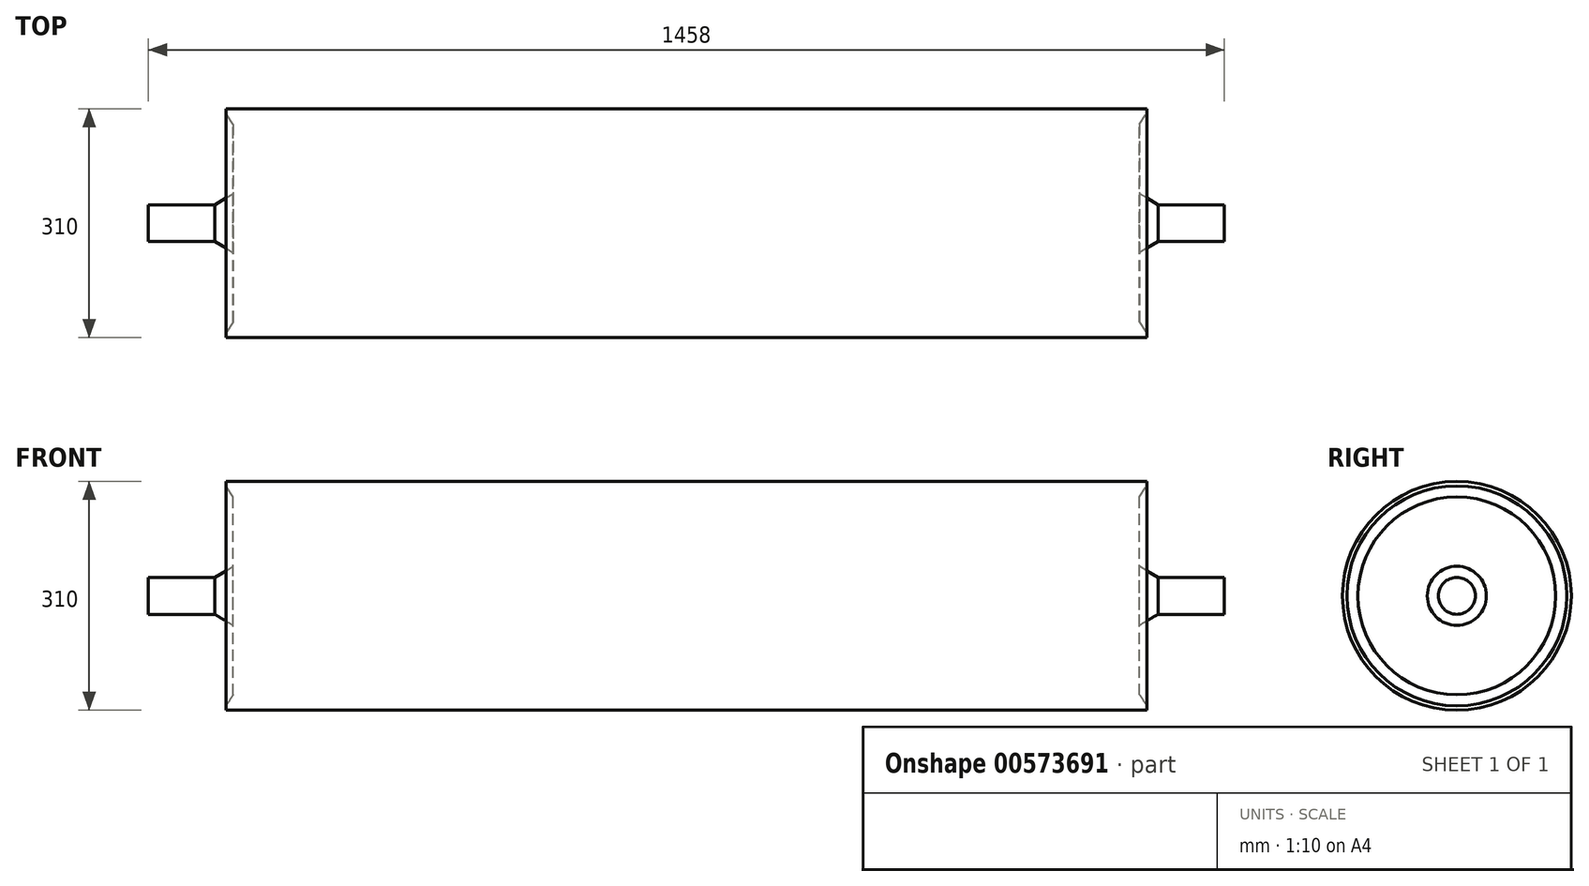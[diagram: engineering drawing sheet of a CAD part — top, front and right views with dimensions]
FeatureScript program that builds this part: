
annotation { "Feature Type Name" : "Feature", "Feature Type Description" : "" }
export const myFeature = defineFeature(function(context is Context, id is Id, definition is map)
    precondition{}
    {
        {
            var Q0;
            Q0=qCreatedBy(makeId("Front.planeOp"),FACE);
            var sketch = newSketch(context, id + "F0", { "sketchPlane" : qUnion([Q0])});
            skLineSegment(sketch, "E0.0", {"start": v(0, 155) * mm, "end": v(-614, 155) * mm});
            skLineSegment(sketch, "E1.0", {"start": v(0, 155) * mm, "end": v(624, 155) * mm});
            skLineSegment(sketch, "E2.0", {"start": v(614, 155) * mm, "end": v(614, 0) * mm});
            skLineSegment(sketch, "E3.0", {"start": v(-614, 155) * mm, "end": v(-614, 0) * mm});
            skLineSegment(sketch, "E4.0", {"start": v(614, 25) * mm, "end": v(729, 25) * mm});
            skLineSegment(sketch, "E5", {"start": v(729, 25) * mm, "end": v(729, 0) * mm});
            skLineSegment(sketch, "E6", {"start": v(614, 40) * mm, "end": v(639, 25) * mm});
            skLineSegment(sketch, "E7.MirrorCS", {"start": v(-614, 25) * mm, "end": v(-729, 25) * mm});
            skLineSegment(sketch, "E8.MirrorCS", {"start": v(-729, 25) * mm, "end": v(-729, 0) * mm});
            skLineSegment(sketch, "E9.MirrorCS", {"start": v(-614, 40) * mm, "end": v(-639, 25) * mm});
            skLineSegment(sketch, "E10", {"start": v(0, 0) * mm, "end": v(-729, 0) * mm});
            skLineSegment(sketch, "E11", {"start": v(0, 0) * mm, "end": v(729, 0) * mm});
            skPoint(sketch, "E12.orphan", {"position": v(-729, -25) * mm});
            skPoint(sketch, "E13.trimOffspring.end.orphan", {"position": v(614, -154.78) * mm});
            skPoint(sketch, "E13.trimOffspring.start.orphan", {"position": v(614, -139.78) * mm});
            skPoint(sketch, "E14.end.orphan", {"position": v(639, -25) * mm});
            skPoint(sketch, "E14.start.orphan", {"position": v(614, -40) * mm});
            skPoint(sketch, "E15.orphan", {"position": v(729, -25) * mm});
            skLineSegment(sketch, "E16", {"start": v(624, 149) * mm, "end": v(614, 134) * mm});
            skLineSegment(sketch, "E17", {"start": v(624, 155) * mm, "end": v(624, 149) * mm});
            skPoint(sketch, "E18.orphan", {"position": v(614, 140) * mm});
            skLineSegment(sketch, "E19", {"start": v(-614, 155) * mm, "end": v(-624, 155) * mm});
            skPoint(sketch, "E20.trimOffspring.end.orphan", {"position": v(-624, 155) * mm});
            skLineSegment(sketch, "E21", {"start": v(-624, 155) * mm, "end": v(-624, 149) * mm});
            skLineSegment(sketch, "E22", {"start": v(-624, 149) * mm, "end": v(-614, 134) * mm});
            skSolve(sketch);
        }
        {
            var Q0;
            Q0 = qSketchRegion(id + "F0", true);
            var Q1;
            Q1=sQuery(id+"F0.wireOp",EDGE,"E10");
            revolve(context, id + "F1", {"entities" : qUnion([Q0]), "axis" : qUnion([Q1]), "revolveType" : RevolveType.FULL});
        }
    });
